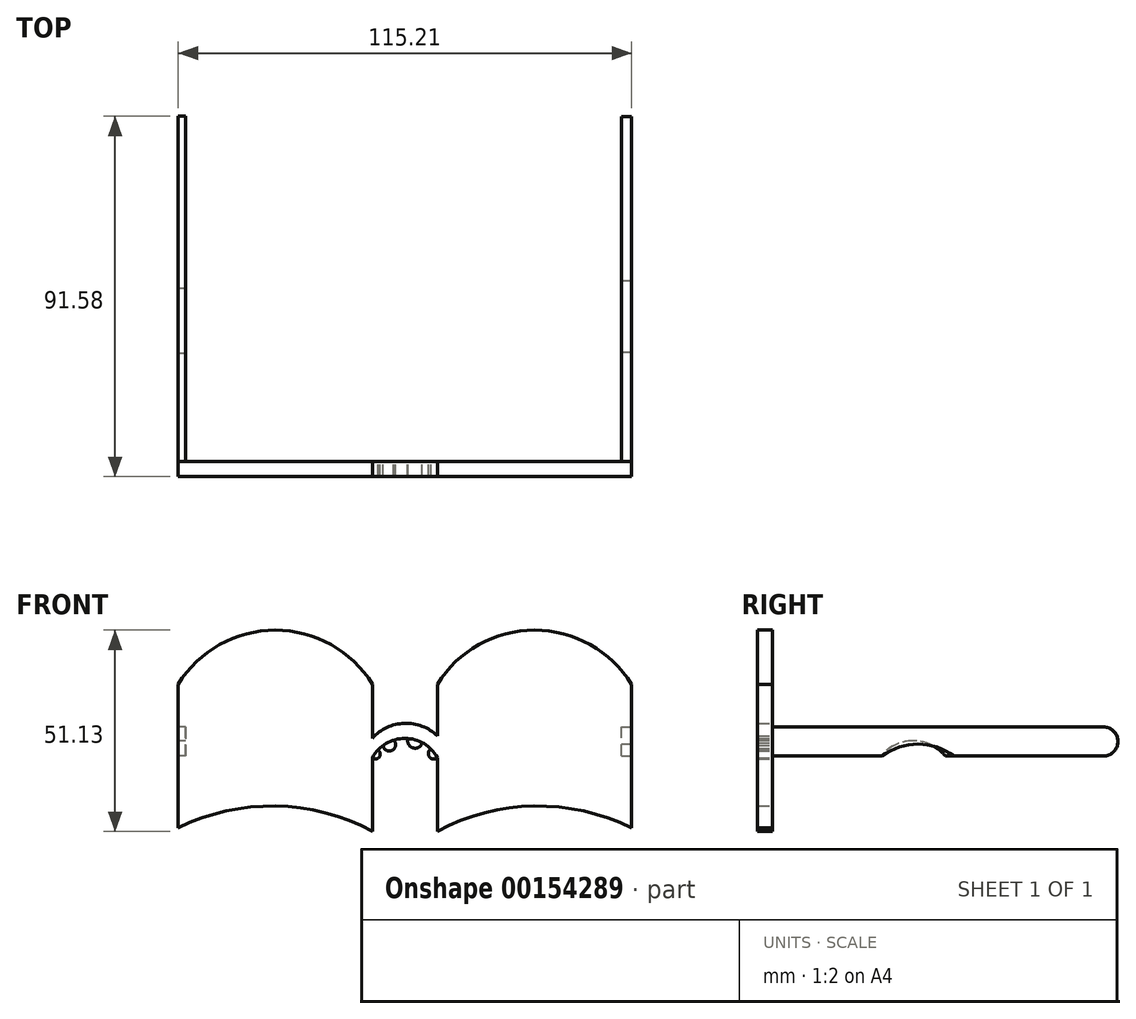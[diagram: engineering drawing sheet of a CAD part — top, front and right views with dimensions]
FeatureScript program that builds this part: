
annotation { "Feature Type Name" : "Feature", "Feature Type Description" : "" }
export const myFeature = defineFeature(function(context is Context, id is Id, definition is map)
    precondition{}
    {
        {
            var Q0;
            Q0=qCreatedBy(makeId("Front.planeOp"),FACE);
            var sketch = newSketch(context, id + "F0", { "sketchPlane" : qUnion([Q0])});
            skArc(sketch, "E0", {"start": v(-19.54, 9.56) * mm, "mid": v(-44.1, 16) * mm, "end": v(-68.89, 10.41) * mm});
            skLineSegment(sketch, "E1", {"start": v(-68.89, 10.41) * mm, "end": v(-68.89, 46.92) * mm});
            skLineSegment(sketch, "E2", {"start": v(-19.54, 9.56) * mm, "end": v(-19.54, 46.92) * mm});
            skArc(sketch, "E3", {"start": v(-19.54, 46.92) * mm, "mid": v(-44.21, 60.7) * mm, "end": v(-68.89, 46.92) * mm});
            skLineSegment(sketch, "E4.MirrorCS", {"start": v(-3.03, 9.56) * mm, "end": v(-3.03, 46.92) * mm});
            skArc(sketch, "E5.MirrorCS", {"start": v(-3.03, 9.56) * mm, "mid": v(21.54, 16) * mm, "end": v(46.32, 10.41) * mm});
            skLineSegment(sketch, "E6.MirrorCS", {"start": v(46.32, 10.41) * mm, "end": v(46.32, 46.92) * mm});
            skArc(sketch, "E7.MirrorCS", {"start": v(-3.03, 46.92) * mm, "mid": v(21.64, 60.7) * mm, "end": v(46.32, 46.92) * mm});
            skArc(sketch, "E8", {"start": v(-3.03, 33.79) * mm, "mid": v(-11.4, 37) * mm, "end": v(-19.54, 33.2) * mm});
            skArc(sketch, "E9", {"start": v(-3.03, 28.24) * mm, "mid": v(-11.29, 33.18) * mm, "end": v(-19.54, 28.24) * mm});
            skSolve(sketch);
        }
        {
            var Q0;
            Q0 = qSketchRegion(id + "F0", true);
            extrude(context, id + "F1", {"entities" : qUnion([Q0]), "depth" : 3.8 * mm});
        }
        {
            var Q0;
            Q0=makeQuery(id+"F1.opExtrude","SWEPT_FACE",FACE,{"disambiguationData":[OSD([sQuery(id+"F0.wireOp",EDGE,"E6.MirrorCS")])]});
            var sketch = newSketch(context, id + "F2", { "sketchPlane" : qUnion([Q0])});
            skLineSegment(sketch, "E10", {"start": v(0, 36.08) * mm, "end": v(27.81, 36.08) * mm});
            skLineSegment(sketch, "E11", {"start": v(0, 28.67) * mm, "end": v(27.81, 28.67) * mm});
            skArc(sketch, "E12", {"start": v(46.07, 28.67) * mm, "mid": v(36.94, 31.73) * mm, "end": v(27.81, 28.67) * mm});
            skLineSegment(sketch, "E13", {"start": v(27.81, 36.08) * mm, "end": v(84, 36.08) * mm});
            skLineSegment(sketch, "E14", {"start": v(46.07, 28.67) * mm, "end": v(84, 28.67) * mm});
            skArc(sketch, "E15", {"start": v(84, 28.67) * mm, "mid": v(87.71, 32.37) * mm, "end": v(84, 36.08) * mm});
            skSolve(sketch);
        }
        {
            var Q0;
            Q0 = qSketchRegion(id + "F2", true);
            var Q1;
            {var subQ1=sQuery(id+"F2.wireOp",EDGE,"E10");Q1=makeQuery(id+"F2.imprint","IMPRINT",FACE,{"disambiguationData":[TD([[makeQuery(id+"F2.imprint","IMPRINT",EDGE,{"derivedFrom":subQ1}),-1.0]])]});}
            extrude(context, id + "F3", {"entities" : qUnion([Q0, Q1]), "oppositeDirection" : true, "depth" : 2.54 * mm});
        }
        {
            var Q0;
            Q0=makeQuery(id+"F1.opExtrude","SWEPT_FACE",FACE,{"disambiguationData":[OSD([sQuery(id+"F0.wireOp",EDGE,"E1")])]});
            var sketch = newSketch(context, id + "F4", { "sketchPlane" : qUnion([Q0])});
            skLineSegment(sketch, "E16", {"start": v(0, 36.08) * mm, "end": v(-84.06, 36.08) * mm});
            skLineSegment(sketch, "E17", {"start": v(0, 28.67) * mm, "end": v(-27.52, 28.67) * mm});
            skArc(sketch, "E18", {"start": v(-27.52, 28.67) * mm, "mid": v(-35.73, 32.57) * mm, "end": v(-43.95, 28.67) * mm});
            skLineSegment(sketch, "E19", {"start": v(-43.95, 28.67) * mm, "end": v(-84.06, 28.67) * mm});
            skArc(sketch, "E20", {"start": v(-84.06, 36.08) * mm, "mid": v(-87.77, 32.37) * mm, "end": v(-84.06, 28.67) * mm});
            skSolve(sketch);
        }
        {
            var Q0;
            Q0 = qSketchRegion(id + "F4", true);
            var Q1;
            {var subQ1=sQuery(id+"F4.wireOp",EDGE,"E16");Q1=makeQuery(id+"F4.imprint","IMPRINT",FACE,{"disambiguationData":[TD([[makeQuery(id+"F4.imprint","IMPRINT",EDGE,{"derivedFrom":subQ1}),1.0]])]});}
            extrude(context, id + "F5", {"entities" : qUnion([Q0, Q1]), "operationType" : NewBodyOperationType.ADD, "oppositeDirection" : true, "depth" : 1.9 * mm});
        }
        {
            var Q0;
            Q0=makeQuery(id+"F1.opExtrude","CAP_FACE",FACE,{"disambiguationData":[OSD([sQuery(id+"F0.wireOp",EDGE,"E0"),sQuery(id+"F0.wireOp",EDGE,"E1"),sQuery(id+"F0.wireOp",EDGE,"E2"),sQuery(id+"F0.wireOp",EDGE,"E3"),sQuery(id+"F0.wireOp",EDGE,"E4.MirrorCS"),sQuery(id+"F0.wireOp",EDGE,"E5.MirrorCS"),sQuery(id+"F0.wireOp",EDGE,"E6.MirrorCS"),sQuery(id+"F0.wireOp",EDGE,"E7.MirrorCS"),sQuery(id+"F0.wireOp",EDGE,"E8"),sQuery(id+"F0.wireOp",EDGE,"E9")])],"isStart":true});
            var sketch = newSketch(context, id + "F6", { "sketchPlane" : qUnion([Q0])});
            skArc(sketch, "E21", {"start": v(3.03, 28.24) * mm, "mid": v(5.05, 28.46) * mm, "end": v(4.68, 30.46) * mm});
            skArc(sketch, "E22", {"start": v(6.88, 32.08) * mm, "mid": v(9.23, 30.76) * mm, "end": v(10.49, 33.15) * mm});
            skArc(sketch, "E23", {"start": v(14.18, 32.72) * mm, "mid": v(14.5, 30.12) * mm, "end": v(16.82, 31.37) * mm});
            skArc(sketch, "E24", {"start": v(18.14, 30.2) * mm, "mid": v(17.77, 28.46) * mm, "end": v(19.54, 28.24) * mm});
            skSolve(sketch);
        }
        {
            var Q0;
            Q0 = qSketchRegion(id + "F6", true);
            var Q1;
            {var subQ0=sQuery(id+"F6.wireOp",EDGE,"E22");Q1=makeQuery(id+"F6.imprint","IMPRINT",FACE,{"disambiguationData":[TD([[makeQuery(id+"F6.imprint","IMPRINT",EDGE,{"derivedFrom":subQ0}),1.0]])]});}
            var Q2;
            {var subQ0=sQuery(id+"F6.wireOp",EDGE,"E21");Q2=makeQuery(id+"F6.imprint","IMPRINT",FACE,{"disambiguationData":[TD([[makeQuery(id+"F6.imprint","IMPRINT",EDGE,{"derivedFrom":subQ0}),1.0]])]});}
            var Q3;
            {var subQ0=sQuery(id+"F6.wireOp",EDGE,"E23");Q3=makeQuery(id+"F6.imprint","IMPRINT",FACE,{"disambiguationData":[TD([[makeQuery(id+"F6.imprint","IMPRINT",EDGE,{"derivedFrom":subQ0}),1.0]])]});}
            var Q4;
            {var subQ0=sQuery(id+"F6.wireOp",EDGE,"E24");Q4=makeQuery(id+"F6.imprint","IMPRINT",FACE,{"disambiguationData":[TD([[makeQuery(id+"F6.imprint","IMPRINT",EDGE,{"derivedFrom":subQ0}),1.0]])]});}
            extrude(context, id + "F7", {"entities" : qUnion([Q0, Q1, Q2, Q3, Q4]), "operationType" : NewBodyOperationType.ADD, "oppositeDirection" : true, "depth" : 3.75 * mm});
        }
    });
